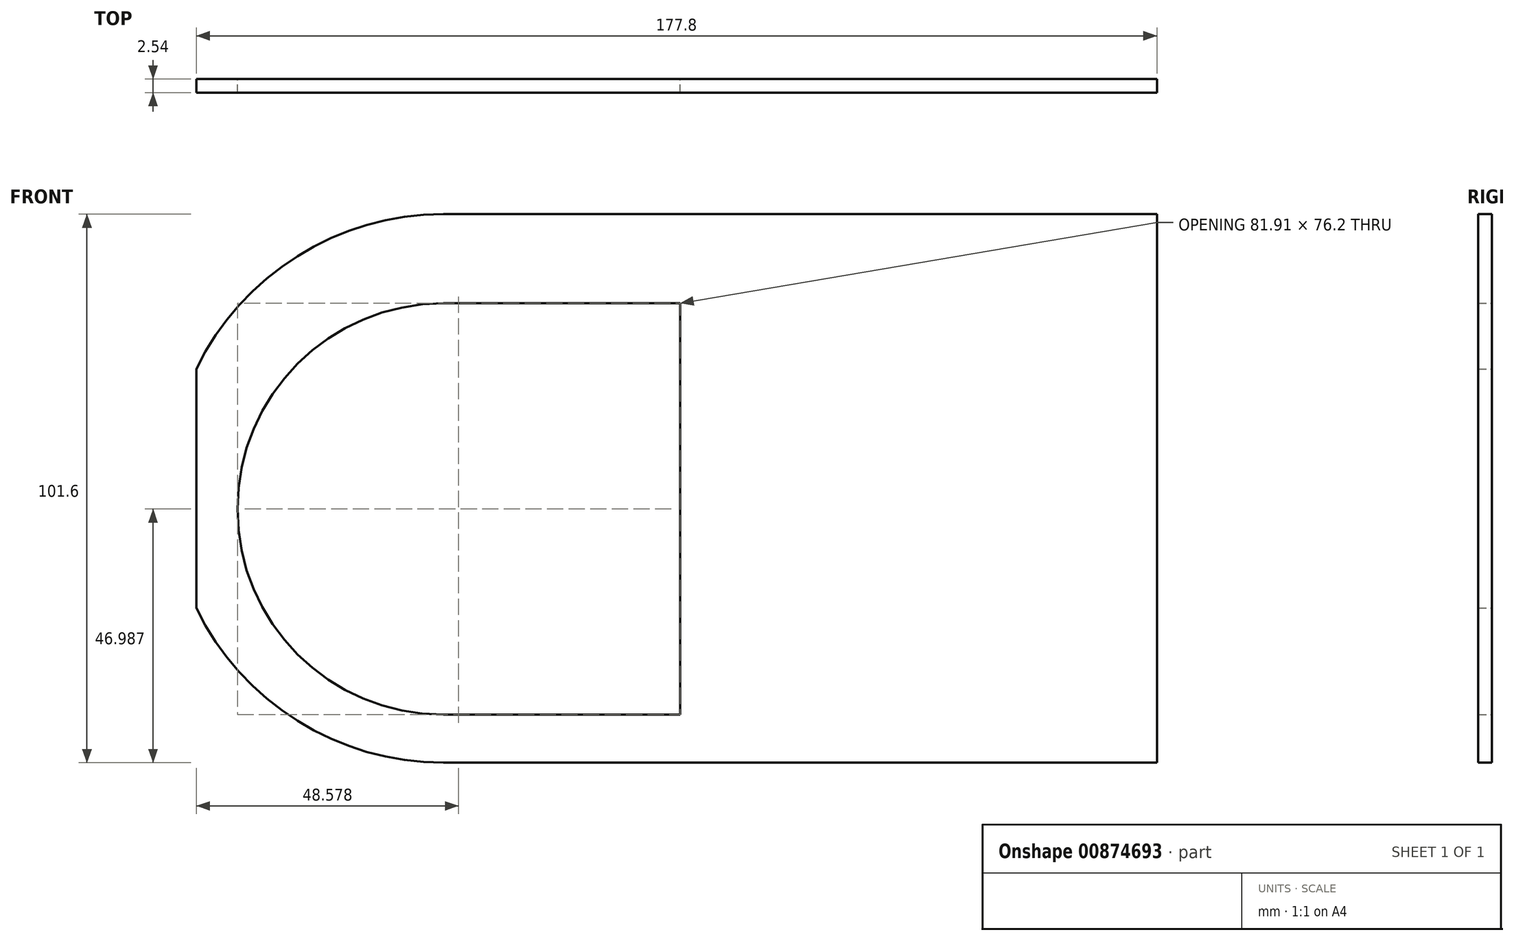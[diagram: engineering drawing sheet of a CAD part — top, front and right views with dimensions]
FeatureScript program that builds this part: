
annotation { "Feature Type Name" : "Feature", "Feature Type Description" : "" }
export const myFeature = defineFeature(function(context is Context, id is Id, definition is map)
    precondition{}
    {
        {
            var Q0;
            Q0=qCreatedBy(makeId("Front.planeOp"),FACE);
            var sketch = newSketch(context, id + "F0", { "sketchPlane" : qUnion([Q0])});
            skArc(sketch, "E0.0", {"start": v(-45.72, -14.87) * mm, "mid": v(-26.98, -35.77) * mm, "end": v(0, -43.52) * mm});
            skLineSegment(sketch, "E1.bottom", {"start": v(0, -43.52) * mm, "end": v(132.08, -43.52) * mm});
            skLineSegment(sketch, "E1.top", {"start": v(0, 58.08) * mm, "end": v(132.08, 58.08) * mm});
            skLineSegment(sketch, "E1.right", {"start": v(132.08, -43.52) * mm, "end": v(132.08, 58.08) * mm});
            skLineSegment(sketch, "E2.right", {"start": v(-45.72, 29.42) * mm, "end": v(-45.72, -14.87) * mm});
            skArc(sketch, "E3.trimOffspring", {"start": v(0, 58.08) * mm, "mid": v(-26.98, 50.32) * mm, "end": v(-45.72, 29.42) * mm});
            skArc(sketch, "E4", {"start": v(0, 41.57) * mm, "mid": v(-38.1, 3.47) * mm, "end": v(0, -34.63) * mm});
            skLineSegment(sketch, "E5", {"start": v(0, 41.57) * mm, "end": v(43.82, 41.57) * mm});
            skLineSegment(sketch, "E6", {"start": v(0, -34.63) * mm, "end": v(43.82, -34.63) * mm});
            skPoint(sketch, "E7.center.orphan", {"position": v(87.63, 3.47) * mm});
            skLineSegment(sketch, "E8", {"start": v(43.81, -34.63) * mm, "end": v(43.81, 41.57) * mm});
            skPoint(sketch, "E9.orphan", {"position": v(87.63, 41.57) * mm});
            skPoint(sketch, "E10.orphan", {"position": v(87.63, -34.63) * mm});
            skCircle(sketch, "E11", {"center": v(0, 3.47) * mm, "radius": 38.1 * mm});
            skSolve(sketch);
        }
        {
            var Q0;
            Q0=qSketchRegion(id+"F0",true);
            extrude(context, id + "F1", {"entities" : qUnion([Q0]), "depth" : 2.54 * mm, "offsetDistance" : 25.4 * mm});
        }
    });
